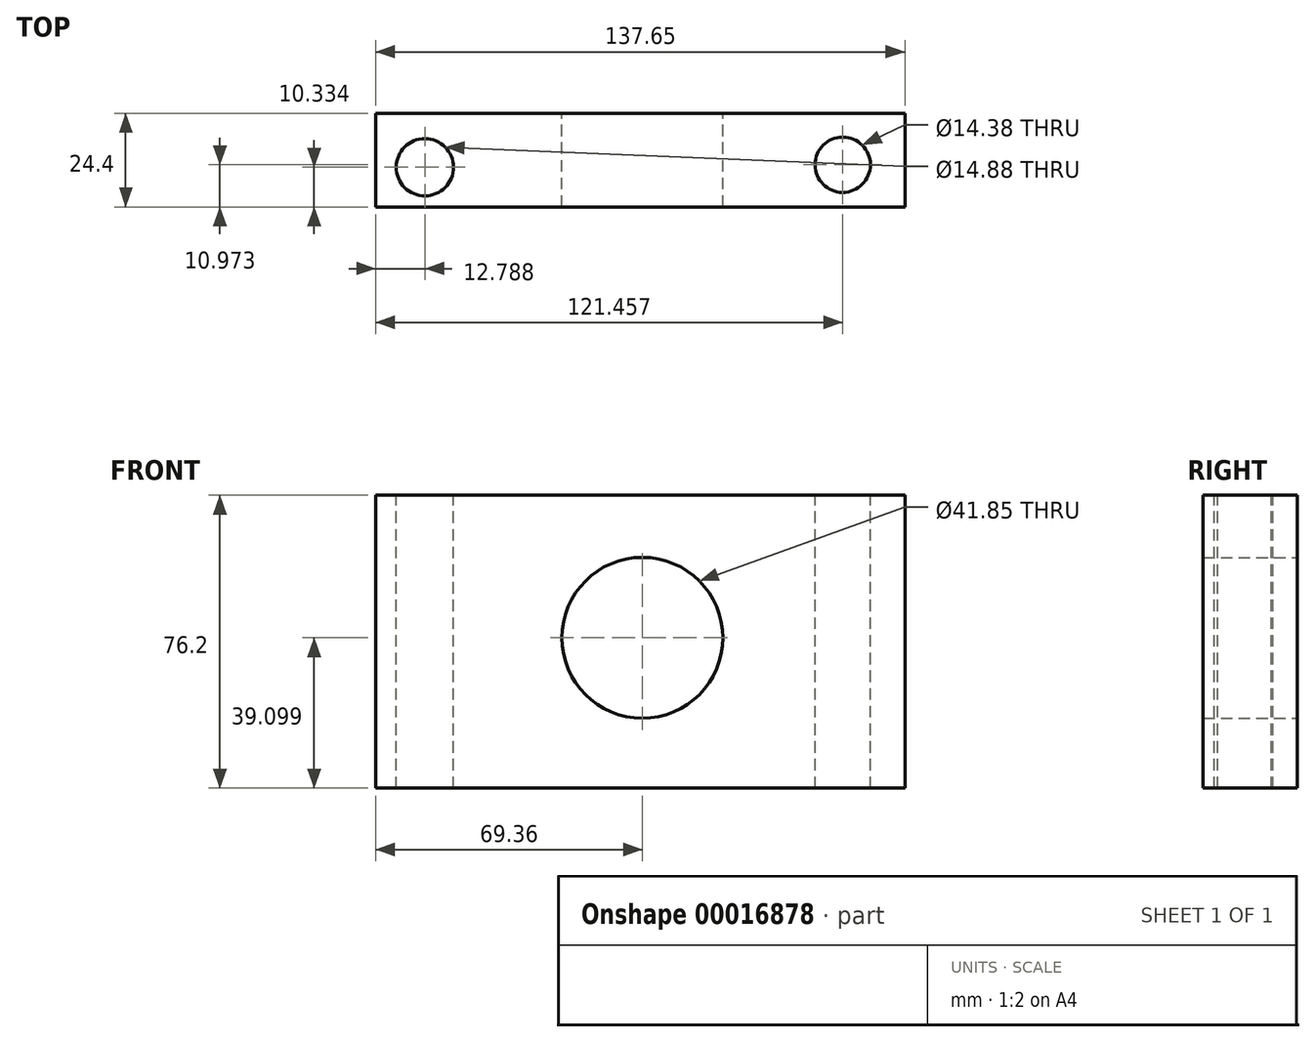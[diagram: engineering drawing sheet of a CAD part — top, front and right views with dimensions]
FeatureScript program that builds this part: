
annotation { "Feature Type Name" : "Feature", "Feature Type Description" : "" }
export const myFeature = defineFeature(function(context is Context, id is Id, definition is map)
    precondition{}
    {
        {
            var Q0;
            Q0=qCreatedBy(makeId("Top.planeOp"),FACE);
            var sketch = newSketch(context, id + "F0", { "sketchPlane" : qUnion([Q0])});
            skLineSegment(sketch, "E0.bottom", {"start": v(-69.36, 24.4) * mm, "end": v(68.3, 24.4) * mm});
            skLineSegment(sketch, "E0.top", {"start": v(-69.36, 0) * mm, "end": v(68.3, 0) * mm});
            skLineSegment(sketch, "E0.left", {"start": v(-69.36, 24.4) * mm, "end": v(-69.36, 0) * mm});
            skLineSegment(sketch, "E0.right", {"start": v(68.3, 24.4) * mm, "end": v(68.3, 0) * mm});
            skSolve(sketch);
        }
        {
            var Q0;
            Q0=makeQuery(id+"F0.imprint","IMPRINT",FACE,{"disambiguationData":[TD([[makeQuery(id+"F0.imprint","IMPRINT",EDGE,{"derivedFrom":sQuery(id+"F0.wireOp",EDGE,"E0.bottom")}),-1.0]])]});
            extrude(context, id + "F1", {"entities" : qUnion([Q0]), "depth" : 76.2 * mm});
        }
        {
            var Q0;
            Q0=makeQuery(id+"F1.opExtrude","SWEPT_FACE",FACE,{"disambiguationData":[OSD([sQuery(id+"F0.wireOp",EDGE,"E0.bottom")])]});
            var sketch = newSketch(context, id + "F2", { "sketchPlane" : qUnion([Q0])});
            skCircle(sketch, "E1", {"center": v(0, 39.1) * mm, "radius": 20.92 * mm});
            skSolve(sketch);
        }
        {
            var Q0;
            Q0=makeQuery(id+"F2.imprint","IMPRINT",FACE,{"disambiguationData":[TD([[makeQuery(id+"F2.imprint","IMPRINT",EDGE,{"derivedFrom":sQuery(id+"F2.wireOp",EDGE,"E1")}),1.0]])]});
            extrude(context, id + "F3", {"entities" : qUnion([Q0]), "operationType" : NewBodyOperationType.REMOVE, "endBound" : BoundingType.THROUGH_ALL, "oppositeDirection" : true, "depth" : 25.4 * mm});
        }
        {
            var Q0;
            Q0=makeQuery(id+"F1.opExtrude","CAP_FACE",FACE,{"disambiguationData":[OSD([sQuery(id+"F0.wireOp",EDGE,"E0.bottom"),sQuery(id+"F0.wireOp",EDGE,"E0.top"),sQuery(id+"F0.wireOp",EDGE,"E0.left"),sQuery(id+"F0.wireOp",EDGE,"E0.right")])],"isStart":false});
            var sketch = newSketch(context, id + "F4", { "sketchPlane" : qUnion([Q0])});
            skCircle(sketch, "E2", {"center": v(-56.57, 10.33) * mm, "radius": 7.44 * mm});
            skCircle(sketch, "E3", {"center": v(52.1, 10.97) * mm, "radius": 7.19 * mm});
            skSolve(sketch);
        }
        {
            var Q0;
            Q0=makeQuery(id+"F4.imprint","IMPRINT",FACE,{"disambiguationData":[TD([[makeQuery(id+"F4.imprint","IMPRINT",EDGE,{"derivedFrom":sQuery(id+"F4.wireOp",EDGE,"E2")}),1.0]])]});
            var Q1;
            Q1=makeQuery(id+"F4.imprint","IMPRINT",FACE,{"disambiguationData":[TD([[makeQuery(id+"F4.imprint","IMPRINT",EDGE,{"derivedFrom":sQuery(id+"F4.wireOp",EDGE,"E3")}),1.0]])]});
            extrude(context, id + "F5", {"entities" : qUnion([Q0, Q1]), "operationType" : NewBodyOperationType.REMOVE, "endBound" : BoundingType.THROUGH_ALL, "oppositeDirection" : true, "depth" : 25.4 * mm});
        }
    });
